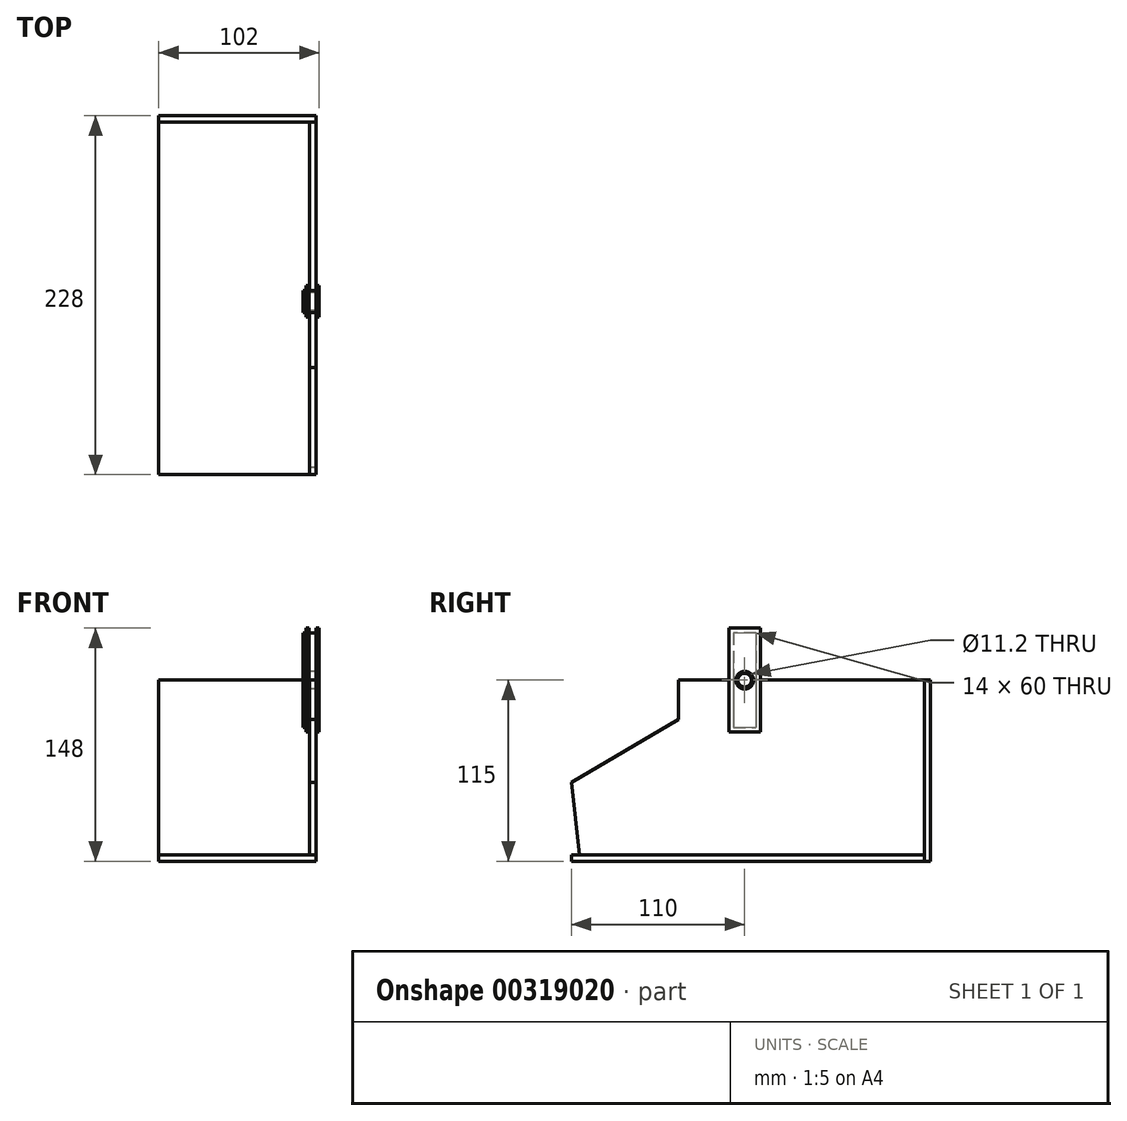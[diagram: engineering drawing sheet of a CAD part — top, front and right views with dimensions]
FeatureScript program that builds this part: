
annotation { "Feature Type Name" : "Feature", "Feature Type Description" : "" }
export const myFeature = defineFeature(function(context is Context, id is Id, definition is map)
    precondition{}
    {
        {
            var Q0;
            Q0=qCreatedBy(makeId("Front.planeOp"),FACE);
            cPlane(context, id + "F0", {"entities" : qUnion([Q0]), "cplaneType" : CPlaneType.OFFSET, "offset" : 110 * mm, "width" : 150 * mm, "height" : 150 * mm});
        }
        {
            var Q0;
            Q0=qCreatedBy(makeId("Top.planeOp"),FACE);
            var sketch = newSketch(context, id + "F1", { "sketchPlane" : qUnion([Q0])});
            skLineSegment(sketch, "E0.0", {"start": v(-50, -110) * mm, "end": v(50, -110) * mm});
            skLineSegment(sketch, "E1.top", {"start": v(-50, 114) * mm, "end": v(50, 114) * mm});
            skLineSegment(sketch, "E1.left", {"start": v(-50, -110) * mm, "end": v(-50, 114) * mm});
            skLineSegment(sketch, "E1.right", {"start": v(50, -110) * mm, "end": v(50, 114) * mm});
            skSolve(sketch);
        }
        {
            var Q0;
            Q0=qSketchRegion(id+"F1",true);
            extrude(context, id + "F2", {"entities" : qUnion([Q0]), "depth" : 4 * mm});
        }
        {
            var Q0;
            Q0=makeQuery(id+"F2.opExtrude","SWEPT_FACE",FACE,{"disambiguationData":[OSD([sQuery(id+"F1.wireOp",EDGE,"E1.top")])]});
            cPlane(context, id + "F3", {"entities" : qUnion([Q0]), "cplaneType" : CPlaneType.OFFSET, "offset" : 4 * mm, "width" : 150 * mm, "height" : 150 * mm});
        }
        {
            var Q0;
            Q0=qCreatedBy(id+"F3.planeOp",FACE);
            var sketch = newSketch(context, id + "F4", { "sketchPlane" : qUnion([Q0])});
            skPoint(sketch, "E2.0", {"position": v(-50, 0) * mm});
            skLineSegment(sketch, "E3.0", {"start": v(50, 0) * mm, "end": v(-50, 0) * mm});
            skPoint(sketch, "E4.0", {"position": v(50, 0) * mm});
            skLineSegment(sketch, "E5.bottom", {"start": v(-50, 0) * mm, "end": v(50, 0) * mm});
            skLineSegment(sketch, "E5.top", {"start": v(-50, 115) * mm, "end": v(50, 115) * mm});
            skLineSegment(sketch, "E5.left", {"start": v(-50, 0) * mm, "end": v(-50, 115) * mm});
            skLineSegment(sketch, "E5.right", {"start": v(50, 0) * mm, "end": v(50, 115) * mm});
            skSolve(sketch);
        }
        {
            var Q0;
            Q0=qSketchRegion(id+"F4",true);
            extrude(context, id + "F5", {"entities" : qUnion([Q0]), "oppositeDirection" : true, "depth" : 4 * mm});
        }
        {
            var Q0;
            Q0=makeQuery(id+"F2.opExtrude","SWEPT_FACE",FACE,{"disambiguationData":[OSD([sQuery(id+"F1.wireOp",EDGE,"E1.right")])]});
            cPlane(context, id + "F6", {"entities" : qUnion([Q0]), "cplaneType" : CPlaneType.OFFSET, "offset" : 0 * mm, "width" : 150 * mm, "height" : 150 * mm});
        }
        {
            var Q0;
            Q0=qCreatedBy(id+"F6.planeOp",FACE);
            var sketch = newSketch(context, id + "F7", { "sketchPlane" : qUnion([Q0])});
            skLineSegment(sketch, "E6.0", {"start": v(-105, 4) * mm, "end": v(114, 4) * mm});
            skLineSegment(sketch, "E7.0", {"start": v(114, 0) * mm, "end": v(114, 115) * mm});
            skLineSegment(sketch, "E8", {"start": v(114, 115) * mm, "end": v(-42, 115) * mm});
            skLineSegment(sketch, "E9", {"start": v(0, 74) * mm, "end": v(0, 4) * mm});
            skLineSegment(sketch, "E10.bottom", {"start": v(-7, 115) * mm, "end": v(7, 115) * mm});
            skLineSegment(sketch, "E10.top", {"start": v(-7, 85) * mm, "end": v(7, 85) * mm});
            skLineSegment(sketch, "E10.left", {"start": v(-7, 115) * mm, "end": v(-7, 85) * mm});
            skLineSegment(sketch, "E10.right", {"start": v(7, 115) * mm, "end": v(7, 85) * mm});
            skLineSegment(sketch, "E11", {"start": v(-42, 115) * mm, "end": v(-42, 90) * mm});
            skLineSegment(sketch, "E12", {"start": v(-42, 90) * mm, "end": v(-110, 50) * mm});
            skLineSegment(sketch, "E13.0", {"start": v(-110, 0) * mm, "end": v(114, 0) * mm});
            skLineSegment(sketch, "E14", {"start": v(-110, 4) * mm, "end": v(-110, 0) * mm});
            skLineSegment(sketch, "E15", {"start": v(-110, 50) * mm, "end": v(-105, 4) * mm});
            skSolve(sketch);
        }
        {
            var Q0;
            {var subQ2=sQuery(id+"F7.wireOp",EDGE,"E6.0");Q0=makeQuery(id+"F7.imprint","IMPRINT",FACE,{"disambiguationData":[TD([[makeQuery(id+"F7.imprint","IMPRINT",EDGE,{"derivedFrom":subQ2}),1.0]])]});}
            extrude(context, id + "F8", {"entities" : qUnion([Q0]), "oppositeDirection" : true, "depth" : 4 * mm});
        }
        {
            var Q0;
            Q0=qCreatedBy(id+"F6.planeOp",FACE);
            var sketch = newSketch(context, id + "F9", { "sketchPlane" : qUnion([Q0])});
            skLineSegment(sketch, "E16.0", {"start": v(-7, 115) * mm, "end": v(-7, 85) * mm});
            skLineSegment(sketch, "E17.0", {"start": v(-7, 115) * mm, "end": v(-51.25, 115) * mm});
            skLineSegment(sketch, "E18.0", {"start": v(114, 115) * mm, "end": v(7, 115) * mm});
            skLineSegment(sketch, "E19.0", {"start": v(7, 115) * mm, "end": v(7, 85) * mm});
            skLineSegment(sketch, "E20.0", {"start": v(-7, 85) * mm, "end": v(7, 85) * mm});
            skLineSegment(sketch, "E21.bottom", {"start": v(-7, 115) * mm, "end": v(7, 115) * mm});
            skCircle(sketch, "E22", {"center": v(0, 115) * mm, "radius": 4.3 * mm});
            skCircle(sketch, "E23", {"center": v(0, 115) * mm, "radius": 5.6 * mm});
            skLineSegment(sketch, "E24", {"start": v(-10, 115) * mm, "end": v(-10, 82) * mm});
            skLineSegment(sketch, "E25", {"start": v(-10, 82) * mm, "end": v(10, 82) * mm});
            skLineSegment(sketch, "E26", {"start": v(10, 82) * mm, "end": v(10, 115) * mm});
            skLineSegment(sketch, "E27", {"start": v(-10, 115) * mm, "end": v(-10, 148) * mm});
            skLineSegment(sketch, "E28", {"start": v(10, 148) * mm, "end": v(10, 115) * mm});
            skLineSegment(sketch, "E29", {"start": v(-10, 148) * mm, "end": v(10, 148) * mm});
            skLineSegment(sketch, "E30", {"start": v(-7, 115) * mm, "end": v(-7, 145) * mm});
            skLineSegment(sketch, "E31", {"start": v(7, 115) * mm, "end": v(7, 145) * mm});
            skLineSegment(sketch, "E32", {"start": v(7, 145) * mm, "end": v(-7, 145) * mm});
            skSolve(sketch);
        }
        {
            var Q0;
            Q0=makeQuery(id+"F9.imprint","IMPRINT",FACE,{"disambiguationData":[TD([[makeQuery(id+"F9.imprint","IMPRINT",EDGE,{"derivedFrom":sQuery(id+"F9.wireOp",EDGE,"E20.0")}),-1.0]])]});
            var Q1;
            Q1=makeQuery(id+"F9.imprint","IMPRINT",FACE,{"disambiguationData":[TD([[makeQuery(id+"F9.imprint","IMPRINT",EDGE,{"derivedFrom":sQuery(id+"F9.wireOp",EDGE,"E20.0")}),1.0]])]});
            var Q2;
            {var subQ0=sQuery(id+"F9.wireOp",EDGE,"E23");var subQ1=sQuery(id+"F9.wireOp",EDGE,"E21.bottom");var subQ2=makeQuery(id+"F9.imprint","INTERSECT",VERTEX,{"disambiguationData":[OD(0.0)],"derivedFrom":[subQ1,subQ0]});Q2=makeQuery(id+"F9.imprint","IMPRINT",FACE,{"disambiguationData":[TD([[makeQuery(id+"F9.imprint","IMPRINT",EDGE,{"disambiguationData":[TD([[subQ2,-1.0]])],"derivedFrom":subQ1}),-1.0]])]});}
            var Q3;
            {var subQ0=sQuery(id+"F9.wireOp",EDGE,"E22");var subQ1=sQuery(id+"F9.wireOp",EDGE,"E21.bottom");var subQ2=makeQuery(id+"F9.imprint","INTERSECT",VERTEX,{"disambiguationData":[OD(0.0)],"derivedFrom":[subQ1,subQ0]});Q3=makeQuery(id+"F9.imprint","IMPRINT",FACE,{"disambiguationData":[TD([[makeQuery(id+"F9.imprint","IMPRINT",EDGE,{"disambiguationData":[TD([[subQ2,-1.0]])],"derivedFrom":subQ1}),-1.0]])]});}
            var Q4;
            {var subQ1=sQuery(id+"F9.wireOp",EDGE,"E27");Q4=makeQuery(id+"F9.imprint","IMPRINT",FACE,{"disambiguationData":[TD([[makeQuery(id+"F9.imprint","IMPRINT",EDGE,{"derivedFrom":subQ1}),-1.0]])]});}
            var Q5;
            {var subQ0=sQuery(id+"F9.wireOp",EDGE,"E30");Q5=makeQuery(id+"F9.imprint","IMPRINT",FACE,{"disambiguationData":[TD([[makeQuery(id+"F9.imprint","IMPRINT",EDGE,{"derivedFrom":subQ0}),-1.0]])]});}
            var Q6;
            {var subQ0=sQuery(id+"F9.wireOp",EDGE,"E23");var subQ1=sQuery(id+"F9.wireOp",EDGE,"E21.bottom");var subQ2=makeQuery(id+"F9.imprint","INTERSECT",VERTEX,{"disambiguationData":[OD(0.0)],"derivedFrom":[subQ1,subQ0]});Q6=makeQuery(id+"F9.imprint","IMPRINT",FACE,{"disambiguationData":[TD([[makeQuery(id+"F9.imprint","IMPRINT",EDGE,{"disambiguationData":[TD([[subQ2,-1.0]])],"derivedFrom":subQ1}),1.0]])]});}
            var Q7;
            {var subQ0=sQuery(id+"F9.wireOp",EDGE,"E22");var subQ1=sQuery(id+"F9.wireOp",EDGE,"E21.bottom");var subQ2=makeQuery(id+"F9.imprint","INTERSECT",VERTEX,{"disambiguationData":[OD(0.0)],"derivedFrom":[subQ1,subQ0]});Q7=makeQuery(id+"F9.imprint","IMPRINT",FACE,{"disambiguationData":[TD([[makeQuery(id+"F9.imprint","IMPRINT",EDGE,{"disambiguationData":[TD([[subQ2,-1.0]])],"derivedFrom":subQ1}),1.0]])]});}
            extrude(context, id + "F10", {"entities" : qUnion([Q0, Q1, Q2, Q3, Q4, Q5, Q6, Q7]), "depth" : 2 * mm, "offsetDistance" : 25 * mm});
        }
        {
            var Q0;
            {var subQ0=sQuery(id+"F9.wireOp",EDGE,"E22");var subQ1=sQuery(id+"F9.wireOp",EDGE,"E21.bottom");var subQ2=makeQuery(id+"F9.imprint","INTERSECT",VERTEX,{"disambiguationData":[OD(0.0)],"derivedFrom":[subQ1,subQ0]});Q0=makeQuery(id+"F9.imprint","IMPRINT",FACE,{"disambiguationData":[TD([[makeQuery(id+"F9.imprint","IMPRINT",EDGE,{"disambiguationData":[TD([[subQ2,-1.0]])],"derivedFrom":subQ1}),-1.0]])]});}
            var Q1;
            {var subQ0=sQuery(id+"F9.wireOp",EDGE,"E22");var subQ1=sQuery(id+"F9.wireOp",EDGE,"E21.bottom");var subQ2=makeQuery(id+"F9.imprint","INTERSECT",VERTEX,{"disambiguationData":[OD(0.0)],"derivedFrom":[subQ1,subQ0]});Q1=makeQuery(id+"F9.imprint","IMPRINT",FACE,{"disambiguationData":[TD([[makeQuery(id+"F9.imprint","IMPRINT",EDGE,{"disambiguationData":[TD([[subQ2,-1.0]])],"derivedFrom":subQ1}),1.0]])]});}
            extrude(context, id + "F11", {"entities" : qUnion([Q0, Q1]), "operationType" : NewBodyOperationType.REMOVE, "oppositeDirection" : true, "depth" : 20 * mm, "offsetDistance" : 25 * mm});
        }
        {
            var Q0;
            {var subQ0=sQuery(id+"F9.wireOp",EDGE,"E23");var subQ1=sQuery(id+"F9.wireOp",EDGE,"E21.bottom");var subQ2=makeQuery(id+"F9.imprint","INTERSECT",VERTEX,{"disambiguationData":[OD(0.0)],"derivedFrom":[subQ1,subQ0]});Q0=makeQuery(id+"F9.imprint","IMPRINT",FACE,{"disambiguationData":[TD([[makeQuery(id+"F9.imprint","IMPRINT",EDGE,{"disambiguationData":[TD([[subQ2,-1.0]])],"derivedFrom":subQ1}),-1.0]])]});}
            var Q1;
            {var subQ0=sQuery(id+"F9.wireOp",EDGE,"E23");var subQ1=sQuery(id+"F9.wireOp",EDGE,"E21.bottom");var subQ2=makeQuery(id+"F9.imprint","INTERSECT",VERTEX,{"disambiguationData":[OD(0.0)],"derivedFrom":[subQ1,subQ0]});Q1=makeQuery(id+"F9.imprint","IMPRINT",FACE,{"disambiguationData":[TD([[makeQuery(id+"F9.imprint","IMPRINT",EDGE,{"disambiguationData":[TD([[subQ2,-1.0]])],"derivedFrom":subQ1}),1.0]])]});}
            extrude(context, id + "F12", {"entities" : qUnion([Q0, Q1]), "operationType" : NewBodyOperationType.ADD, "oppositeDirection" : true, "depth" : 8.15 * mm, "offsetDistance" : 25 * mm});
        }
        {
            var Q0;
            Q0=makeQuery(id+"F9.imprint","IMPRINT",FACE,{"disambiguationData":[TD([[makeQuery(id+"F9.imprint","IMPRINT",EDGE,{"derivedFrom":sQuery(id+"F9.wireOp",EDGE,"E20.0")}),1.0]])]});
            var Q1;
            {var subQ0=sQuery(id+"F9.wireOp",EDGE,"E30");Q1=makeQuery(id+"F9.imprint","IMPRINT",FACE,{"disambiguationData":[TD([[makeQuery(id+"F9.imprint","IMPRINT",EDGE,{"derivedFrom":subQ0}),-1.0]])]});}
            extrude(context, id + "F13", {"entities" : qUnion([Q0, Q1]), "operationType" : NewBodyOperationType.ADD, "oppositeDirection" : true, "depth" : 4.45 * mm, "offsetDistance" : 25 * mm});
        }
        {
            var Q0;
            Q0=makeQuery(id+"F8.opExtrude","CAP_FACE",FACE,{"disambiguationData":[OSD([sQuery(id+"F7.wireOp",EDGE,"E6.0"),sQuery(id+"F7.wireOp",EDGE,"E7.0"),sQuery(id+"F7.wireOp",EDGE,"E8"),sQuery(id+"F7.wireOp",EDGE,"E10.top"),sQuery(id+"F7.wireOp",EDGE,"E10.left"),sQuery(id+"F7.wireOp",EDGE,"E10.right"),sQuery(id+"F7.wireOp",EDGE,"E11"),sQuery(id+"F7.wireOp",EDGE,"E12"),sQuery(id+"F7.wireOp",EDGE,"E15")])],"isStart":false});
            cPlane(context, id + "F14", {"entities" : qUnion([Q0]), "cplaneType" : CPlaneType.OFFSET, "offset" : 0.35 * mm, "width" : 150 * mm, "height" : 150 * mm});
        }
        {
            var Q0;
            Q0=qCreatedBy(id+"F14.planeOp",FACE);
            var sketch = newSketch(context, id + "F15", { "sketchPlane" : qUnion([Q0])});
            skLineSegment(sketch, "E33.0", {"start": v(-10, 82) * mm, "end": v(-10, 115) * mm});
            skLineSegment(sketch, "E34.0", {"start": v(10, 82) * mm, "end": v(-10, 82) * mm});
            skLineSegment(sketch, "E35.0", {"start": v(10, 115) * mm, "end": v(10, 82) * mm});
            skLineSegment(sketch, "E36.0", {"start": v(-10, 148) * mm, "end": v(-10, 115) * mm});
            skLineSegment(sketch, "E37.0", {"start": v(10, 148) * mm, "end": v(-10, 148) * mm});
            skLineSegment(sketch, "E38.0", {"start": v(10, 115) * mm, "end": v(10, 148) * mm});
            skLineSegment(sketch, "E39.0", {"start": v(7, 115) * mm, "end": v(7, 145) * mm});
            skLineSegment(sketch, "E40.0", {"start": v(-7, 145) * mm, "end": v(7, 145) * mm});
            skLineSegment(sketch, "E41.0", {"start": v(-7, 115) * mm, "end": v(-7, 145) * mm});
            skLineSegment(sketch, "E42.0", {"start": v(-114, 115) * mm, "end": v(-7, 115) * mm});
            skLineSegment(sketch, "E43.0", {"start": v(7, 115) * mm, "end": v(51.25, 115) * mm});
            skCircle(sketch, "E44.0", {"center": v(0, 115) * mm, "radius": 4.3 * mm});
            skCircle(sketch, "E45.0", {"center": v(0, 115) * mm, "radius": 5.6 * mm});
            skLineSegment(sketch, "E46.0", {"start": v(7, 115) * mm, "end": v(10, 115) * mm});
            skLineSegment(sketch, "E47.0", {"start": v(-10, 115) * mm, "end": v(-7, 115) * mm});
            skLineSegment(sketch, "E48.0", {"start": v(-4, 115) * mm, "end": v(-5.35, 115) * mm});
            skLineSegment(sketch, "E49.0", {"start": v(5.35, 115) * mm, "end": v(4, 115) * mm});
            skLineSegment(sketch, "E50.0", {"start": v(-4, 115) * mm, "end": v(4, 115) * mm});
            skLineSegment(sketch, "E51", {"start": v(-7, 115) * mm, "end": v(-5.35, 115) * mm});
            skLineSegment(sketch, "E52", {"start": v(5.35, 115) * mm, "end": v(7, 115) * mm});
            skSolve(sketch);
        }
        {
            var Q0;
            Q0=makeQuery(id+"F15.imprint","IMPRINT",FACE,{"disambiguationData":[TD([[makeQuery(id+"F15.imprint","IMPRINT",EDGE,{"derivedFrom":sQuery(id+"F15.wireOp",EDGE,"E33.0")}),-1.0]])]});
            var Q1;
            Q1=makeQuery(id+"F15.imprint","IMPRINT",FACE,{"disambiguationData":[TD([[makeQuery(id+"F15.imprint","IMPRINT",EDGE,{"derivedFrom":sQuery(id+"F15.wireOp",EDGE,"E36.0")}),1.0]])]});
            var Q2;
            Q2=makeQuery(id+"F15.imprint","IMPRINT",FACE,{"disambiguationData":[TD([[makeQuery(id+"F15.imprint","IMPRINT",EDGE,{"derivedFrom":sQuery(id+"F15.wireOp",EDGE,"E39.0")}),1.0]])]});
            extrude(context, id + "F16", {"entities" : qUnion([Q0, Q1, Q2]), "operationType" : NewBodyOperationType.ADD, "depth" : 2 * mm});
        }
        {
            var Q0;
            {var subQ0=sQuery(id+"F9.wireOp",EDGE,"E22");var subQ1=sQuery(id+"F9.wireOp",EDGE,"E21.bottom");var subQ2=makeQuery(id+"F9.imprint","INTERSECT",VERTEX,{"disambiguationData":[OD(0.0)],"derivedFrom":[subQ1,subQ0]});Q0=makeQuery(id+"F9.imprint","IMPRINT",FACE,{"disambiguationData":[TD([[makeQuery(id+"F9.imprint","IMPRINT",EDGE,{"disambiguationData":[TD([[subQ2,-1.0]])],"derivedFrom":subQ1}),-1.0]])]});}
            var Q1;
            {var subQ0=sQuery(id+"F9.wireOp",EDGE,"E22");var subQ1=sQuery(id+"F9.wireOp",EDGE,"E21.bottom");var subQ2=makeQuery(id+"F9.imprint","INTERSECT",VERTEX,{"disambiguationData":[OD(0.0)],"derivedFrom":[subQ1,subQ0]});Q1=makeQuery(id+"F9.imprint","IMPRINT",FACE,{"disambiguationData":[TD([[makeQuery(id+"F9.imprint","IMPRINT",EDGE,{"disambiguationData":[TD([[subQ2,-1.0]])],"derivedFrom":subQ1}),1.0]])]});}
            extrude(context, id + "F17", {"entities" : qUnion([Q0, Q1]), "operationType" : NewBodyOperationType.REMOVE, "depth" : 0.6 * mm});
        }
    });
